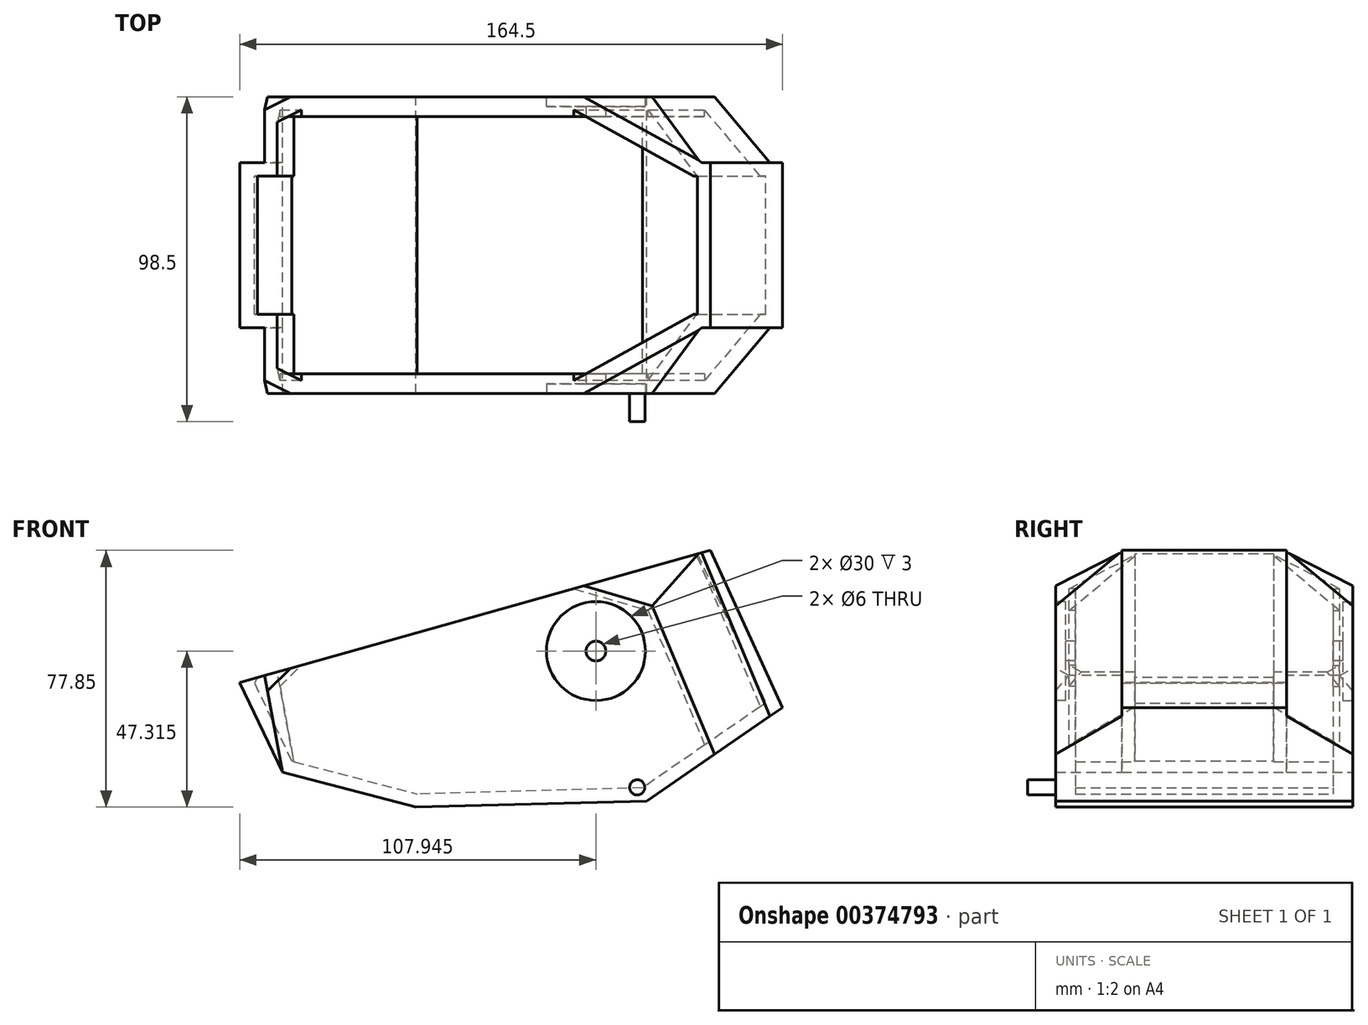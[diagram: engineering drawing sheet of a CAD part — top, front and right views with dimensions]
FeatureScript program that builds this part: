
annotation { "Feature Type Name" : "Feature", "Feature Type Description" : "" }
export const myFeature = defineFeature(function(context is Context, id is Id, definition is map)
    precondition{}
    {
        {
            var Q0;
            Q0=qCreatedBy(makeId("Front.planeOp"),FACE);
            var sketch = newSketch(context, id + "F0", { "sketchPlane" : qUnion([Q0])});
            skLineSegment(sketch, "E0", {"start": v(59.84, 44.16) * mm, "end": v(16.91, 57.67) * mm});
            skLineSegment(sketch, "E1", {"start": v(16.91, 57.67) * mm, "end": v(-68.9, 30.57) * mm});
            skLineSegment(sketch, "E2", {"start": v(-68.9, 30.57) * mm, "end": v(-82.75, 3.95) * mm});
            skLineSegment(sketch, "E3", {"start": v(-82.75, 3.95) * mm, "end": v(-69.82, -23.12) * mm});
            skLineSegment(sketch, "E4", {"start": v(-69.82, -23.12) * mm, "end": v(-29.42, -33.71) * mm});
            skLineSegment(sketch, "E5", {"start": v(59.84, 44.16) * mm, "end": v(-82.75, 3.95) * mm});
            skLineSegment(sketch, "E6", {"start": v(59.84, 44.16) * mm, "end": v(-205.25, -30.6) * mm, "construction": true});
            skLineSegment(sketch, "E7", {"start": v(81.75, -3.5) * mm, "end": v(40.56, -31.85) * mm});
            skLineSegment(sketch, "E8", {"start": v(59.84, 44.16) * mm, "end": v(81.75, -3.5) * mm});
            skLineSegment(sketch, "E9", {"start": v(40.56, -31.85) * mm, "end": v(-29.42, -33.71) * mm});
            skPoint(sketch, "E10", {"position": v(57.24, -20.37) * mm});
            skSolve(sketch);
        }
        {
            var Q0;
            Q0 = qSketchRegion(id + "F0", true);
            extrude(context, id + "F1", {"entities" : qUnion([Q0]), "depth" : 50 * mm, "offsetDistance" : 25 * mm});
        }
        {
            var Q0;
            Q0=makeQuery(id+"F1.opExtrude","CAP_FACE",FACE,{"disambiguationData":[OSD([sQuery(id+"F0.wireOp",EDGE,"bDbODIuM-1u16-Aznj-rPBm-DqaUrzULmyHa"),sQuery(id+"F0.wireOp",EDGE,"UB7G52HZ-YFA2-uVYt-4jSg-YKdLqot3CmFC"),sQuery(id+"F0.wireOp",EDGE,"E0"),sQuery(id+"F0.wireOp",EDGE,"E1"),sQuery(id+"F0.wireOp",EDGE,"E2"),sQuery(id+"F0.wireOp",EDGE,"E3"),sQuery(id+"F0.wireOp",EDGE,"evsTFQqy-KAtR-kOSi-w0PH-wNtTzoorWs0J"),sQuery(id+"F0.wireOp",EDGE,"E4")])],"isStart":false});
            var sketch = newSketch(context, id + "F2", { "sketchPlane" : qUnion([Q0])});
            skLineSegment(sketch, "E11", {"start": v(-69.82, -23.12) * mm, "end": v(61.15, -17.68) * mm, "construction": true});
            skLineSegment(sketch, "E12", {"start": v(61.15, -17.68) * mm, "end": v(42.24, 27.3) * mm});
            skLineSegment(sketch, "E13", {"start": v(42.24, 27.3) * mm, "end": v(9.45, 36.88) * mm});
            skLineSegment(sketch, "E14", {"start": v(9.45, 36.88) * mm, "end": v(-60.14, 15.5) * mm});
            skLineSegment(sketch, "E15", {"start": v(-60.14, 15.5) * mm, "end": v(-74.38, 1.46) * mm});
            skLineSegment(sketch, "E16", {"start": v(-74.38, 1.46) * mm, "end": v(-69.82, -23.12) * mm});
            skSolve(sketch);
        }
        {
            var Q0;
            Q0=makeQuery(id+"F2.imprint","IMPRINT",FACE,{"disambiguationData":[TD([[makeQuery(id+"F2.imprint","IMPRINT",EDGE,{"derivedFrom":sQuery(id+"F2.wireOp",EDGE,"E12")}),1.0]])]});
            extrude(context, id + "F3", {"entities" : qUnion([Q0]), "operationType" : NewBodyOperationType.ADD, "depth" : 20 * mm, "offsetDistance" : 25 * mm, "hasSecondDirection" : true, "secondDirectionOppositeDirection" : true, "secondDirectionDepth" : (20 + 50) * mm});
        }
        {
            var Q0;
            Q0=makeQuery(id+"F3.boolean.opBoolean","INTERSECT",EDGE,{"derivedFrom":[makeQuery(id+"F1.opExtrude","CAP_FACE",FACE,{"disambiguationData":[OSD([sQuery(id+"F0.wireOp",EDGE,"bDbODIuM-1u16-Aznj-rPBm-DqaUrzULmyHa"),sQuery(id+"F0.wireOp",EDGE,"UB7G52HZ-YFA2-uVYt-4jSg-YKdLqot3CmFC"),sQuery(id+"F0.wireOp",EDGE,"E0"),sQuery(id+"F0.wireOp",EDGE,"E1"),sQuery(id+"F0.wireOp",EDGE,"E2"),sQuery(id+"F0.wireOp",EDGE,"E3"),sQuery(id+"F0.wireOp",EDGE,"evsTFQqy-KAtR-kOSi-w0PH-wNtTzoorWs0J"),sQuery(id+"F0.wireOp",EDGE,"E4")])],"isStart":true}),makeQuery(id+"F3.opExtrude","SWEPT_FACE",FACE,{"disambiguationData":[OSD([sQuery(id+"F2.wireOp",EDGE,"E14")])]})]});
            var Q1;
            Q1=makeQuery(id+"F3.boolean.opBoolean","INTERSECT",EDGE,{"derivedFrom":[makeQuery(id+"F1.opExtrude","CAP_FACE",FACE,{"disambiguationData":[OSD([sQuery(id+"F0.wireOp",EDGE,"bDbODIuM-1u16-Aznj-rPBm-DqaUrzULmyHa"),sQuery(id+"F0.wireOp",EDGE,"UB7G52HZ-YFA2-uVYt-4jSg-YKdLqot3CmFC"),sQuery(id+"F0.wireOp",EDGE,"E0"),sQuery(id+"F0.wireOp",EDGE,"E1"),sQuery(id+"F0.wireOp",EDGE,"E2"),sQuery(id+"F0.wireOp",EDGE,"E3"),sQuery(id+"F0.wireOp",EDGE,"evsTFQqy-KAtR-kOSi-w0PH-wNtTzoorWs0J"),sQuery(id+"F0.wireOp",EDGE,"E4")])],"isStart":true}),makeQuery(id+"F3.opExtrude","SWEPT_FACE",FACE,{"disambiguationData":[OSD([sQuery(id+"F2.wireOp",EDGE,"E13")])]})]});
            var Q2;
            Q2=makeQuery(id+"F3.boolean.opBoolean","INTERSECT",EDGE,{"derivedFrom":[makeQuery(id+"F1.opExtrude","CAP_FACE",FACE,{"disambiguationData":[OSD([sQuery(id+"F0.wireOp",EDGE,"bDbODIuM-1u16-Aznj-rPBm-DqaUrzULmyHa"),sQuery(id+"F0.wireOp",EDGE,"UB7G52HZ-YFA2-uVYt-4jSg-YKdLqot3CmFC"),sQuery(id+"F0.wireOp",EDGE,"E0"),sQuery(id+"F0.wireOp",EDGE,"E1"),sQuery(id+"F0.wireOp",EDGE,"E2"),sQuery(id+"F0.wireOp",EDGE,"E3"),sQuery(id+"F0.wireOp",EDGE,"evsTFQqy-KAtR-kOSi-w0PH-wNtTzoorWs0J"),sQuery(id+"F0.wireOp",EDGE,"E4")])],"isStart":true}),makeQuery(id+"F3.opExtrude","SWEPT_FACE",FACE,{"disambiguationData":[OSD([sQuery(id+"F2.wireOp",EDGE,"E15")])]})]});
            var Q3;
            Q3=makeQuery(id+"F3.boolean.opBoolean","INTERSECT",EDGE,{"derivedFrom":[makeQuery(id+"F1.opExtrude","CAP_FACE",FACE,{"disambiguationData":[OSD([sQuery(id+"F0.wireOp",EDGE,"bDbODIuM-1u16-Aznj-rPBm-DqaUrzULmyHa"),sQuery(id+"F0.wireOp",EDGE,"UB7G52HZ-YFA2-uVYt-4jSg-YKdLqot3CmFC"),sQuery(id+"F0.wireOp",EDGE,"E0"),sQuery(id+"F0.wireOp",EDGE,"E1"),sQuery(id+"F0.wireOp",EDGE,"E2"),sQuery(id+"F0.wireOp",EDGE,"E3"),sQuery(id+"F0.wireOp",EDGE,"evsTFQqy-KAtR-kOSi-w0PH-wNtTzoorWs0J"),sQuery(id+"F0.wireOp",EDGE,"E4")])],"isStart":true}),makeQuery(id+"F3.opExtrude","SWEPT_FACE",FACE,{"disambiguationData":[OSD([sQuery(id+"F2.wireOp",EDGE,"E12")])]})]});
            chamfer(context, id + "F4", {"entities" : qUnion([Q0, Q1, Q2, Q3]), "chamferType" : ChamferType.OFFSET_ANGLE, "width" : 20 * mm, "oppositeDirection" : false, "angle" : 45 * degree, "tangentPropagation" : true});
        }
        {
            var Q0;
            Q0=makeQuery(id+"F3.boolean.opBoolean","INTERSECT",EDGE,{"derivedFrom":[makeQuery(id+"F1.opExtrude","CAP_FACE",FACE,{"disambiguationData":[OSD([sQuery(id+"F0.wireOp",EDGE,"bDbODIuM-1u16-Aznj-rPBm-DqaUrzULmyHa"),sQuery(id+"F0.wireOp",EDGE,"UB7G52HZ-YFA2-uVYt-4jSg-YKdLqot3CmFC"),sQuery(id+"F0.wireOp",EDGE,"E0"),sQuery(id+"F0.wireOp",EDGE,"E1"),sQuery(id+"F0.wireOp",EDGE,"E2"),sQuery(id+"F0.wireOp",EDGE,"E3"),sQuery(id+"F0.wireOp",EDGE,"evsTFQqy-KAtR-kOSi-w0PH-wNtTzoorWs0J"),sQuery(id+"F0.wireOp",EDGE,"E4")])],"isStart":false}),makeQuery(id+"F3.opExtrude","SWEPT_FACE",FACE,{"disambiguationData":[OSD([sQuery(id+"F2.wireOp",EDGE,"E13")])]})]});
            var Q1;
            Q1=makeQuery(id+"F3.boolean.opBoolean","INTERSECT",EDGE,{"derivedFrom":[makeQuery(id+"F1.opExtrude","CAP_FACE",FACE,{"disambiguationData":[OSD([sQuery(id+"F0.wireOp",EDGE,"bDbODIuM-1u16-Aznj-rPBm-DqaUrzULmyHa"),sQuery(id+"F0.wireOp",EDGE,"UB7G52HZ-YFA2-uVYt-4jSg-YKdLqot3CmFC"),sQuery(id+"F0.wireOp",EDGE,"E0"),sQuery(id+"F0.wireOp",EDGE,"E1"),sQuery(id+"F0.wireOp",EDGE,"E2"),sQuery(id+"F0.wireOp",EDGE,"E3"),sQuery(id+"F0.wireOp",EDGE,"evsTFQqy-KAtR-kOSi-w0PH-wNtTzoorWs0J"),sQuery(id+"F0.wireOp",EDGE,"E4")])],"isStart":false}),makeQuery(id+"F3.opExtrude","SWEPT_FACE",FACE,{"disambiguationData":[OSD([sQuery(id+"F2.wireOp",EDGE,"E14")])]})]});
            var Q2;
            Q2=makeQuery(id+"F3.boolean.opBoolean","INTERSECT",EDGE,{"derivedFrom":[makeQuery(id+"F1.opExtrude","CAP_FACE",FACE,{"disambiguationData":[OSD([sQuery(id+"F0.wireOp",EDGE,"bDbODIuM-1u16-Aznj-rPBm-DqaUrzULmyHa"),sQuery(id+"F0.wireOp",EDGE,"UB7G52HZ-YFA2-uVYt-4jSg-YKdLqot3CmFC"),sQuery(id+"F0.wireOp",EDGE,"E0"),sQuery(id+"F0.wireOp",EDGE,"E1"),sQuery(id+"F0.wireOp",EDGE,"E2"),sQuery(id+"F0.wireOp",EDGE,"E3"),sQuery(id+"F0.wireOp",EDGE,"evsTFQqy-KAtR-kOSi-w0PH-wNtTzoorWs0J"),sQuery(id+"F0.wireOp",EDGE,"E4")])],"isStart":false}),makeQuery(id+"F3.opExtrude","SWEPT_FACE",FACE,{"disambiguationData":[OSD([sQuery(id+"F2.wireOp",EDGE,"E12")])]})]});
            var Q3;
            Q3=makeQuery(id+"F3.boolean.opBoolean","INTERSECT",EDGE,{"derivedFrom":[makeQuery(id+"F1.opExtrude","CAP_FACE",FACE,{"disambiguationData":[OSD([sQuery(id+"F0.wireOp",EDGE,"bDbODIuM-1u16-Aznj-rPBm-DqaUrzULmyHa"),sQuery(id+"F0.wireOp",EDGE,"UB7G52HZ-YFA2-uVYt-4jSg-YKdLqot3CmFC"),sQuery(id+"F0.wireOp",EDGE,"E0"),sQuery(id+"F0.wireOp",EDGE,"E1"),sQuery(id+"F0.wireOp",EDGE,"E2"),sQuery(id+"F0.wireOp",EDGE,"E3"),sQuery(id+"F0.wireOp",EDGE,"evsTFQqy-KAtR-kOSi-w0PH-wNtTzoorWs0J"),sQuery(id+"F0.wireOp",EDGE,"E4")])],"isStart":false}),makeQuery(id+"F3.opExtrude","SWEPT_FACE",FACE,{"disambiguationData":[OSD([sQuery(id+"F2.wireOp",EDGE,"E15")])]})]});
            chamfer(context, id + "F5", {"entities" : qUnion([Q0, Q1, Q2, Q3]), "chamferType" : ChamferType.OFFSET_ANGLE, "width" : 20 * mm, "oppositeDirection" : false, "angle" : 45 * degree, "tangentPropagation" : true});
        }
        {
            var Q0;
            Q0=makeQuery(id+"F1.opExtrude","SWEPT_EDGE",EDGE,{"disambiguationData":[OSD([sQuery(id+"F0.wireOp",EDGE,"E0"),sQuery(id+"F0.wireOp",EDGE,"E1")])]});
            cPlane(context, id + "F6", {"entities" : qUnion([Q0]), "cplaneType" : CPlaneType.MID_PLANE, "offset" : 25 * mm, "width" : 150 * mm, "height" : 150 * mm});
        }
        {
            var Q0;
            Q0=qCreatedBy(id+"F6.planeOp",FACE);
            var sketch = newSketch(context, id + "F7", { "sketchPlane" : qUnion([Q0])});
            skLineSegment(sketch, "E17", {"start": v(107.63, -2.94) * mm, "end": v(-40.6, 38.73) * mm});
            skLineSegment(sketch, "E18", {"start": v(-40.6, 38.73) * mm, "end": v(-63.04, 45.04) * mm});
            skLineSegment(sketch, "E19", {"start": v(-63.04, 45.04) * mm, "end": v(41.08, 93.89) * mm});
            skLineSegment(sketch, "E20", {"start": v(41.08, 93.89) * mm, "end": v(107.63, -2.94) * mm});
            skSolve(sketch);
        }
        {
            var Q0;
            Q0=makeQuery(id+"F7.imprint","IMPRINT",FACE,{"disambiguationData":[TD([[makeQuery(id+"F7.imprint","IMPRINT",EDGE,{"derivedFrom":sQuery(id+"F7.wireOp",EDGE,"E17")}),-1.0]])]});
            extrude(context, id + "F8", {"entities" : qUnion([Q0]), "operationType" : NewBodyOperationType.REMOVE, "oppositeDirection" : true, "depth" : 56 * mm, "offsetDistance" : 25 * mm, "hasSecondDirection" : true, "secondDirectionOppositeDirection" : false, "secondDirectionDepth" : 80 * mm});
        }
        {
            var Q0;
            Q0=makeQuery(id+"F8.boolean.opBoolean","COPY",FACE,{"derivedFrom":makeQuery(id+"F8.opExtrude","SWEPT_FACE",FACE,{"disambiguationData":[OSD([sQuery(id+"F7.wireOp",EDGE,"E17"),sQuery(id+"F7.wireOp",EDGE,"E18")])]})});
            shell(context, id + "F9", {"entities" : qUnion([Q0]), "thickness" : 4 * mm});
        }
        {
            var Q0;
            Q0=makeQuery(id+"F3.opExtrude","CAP_FACE",FACE,{"disambiguationData":[OSD([sQuery(id+"F0.wireOp",EDGE,"E4"),sQuery(id+"F0.wireOp",EDGE,"E7"),sQuery(id+"F0.wireOp",EDGE,"E9"),sQuery(id+"F2.wireOp",EDGE,"E12"),sQuery(id+"F2.wireOp",EDGE,"E13"),sQuery(id+"F2.wireOp",EDGE,"E14"),sQuery(id+"F2.wireOp",EDGE,"E15"),sQuery(id+"F2.wireOp",EDGE,"E16")])],"isStart":true});
            var sketch = newSketch(context, id + "F10", { "sketchPlane" : qUnion([Q0])});
            skLineSegment(sketch, "E21", {"start": v(-21.5, 33.36) * mm, "end": v(-40.56, -31.85) * mm, "construction": true});
            skPoint(sketch, "E22", {"position": v(-27.11, 14.17) * mm});
            skLineSegment(sketch, "E23", {"start": v(-27.11, 14.17) * mm, "end": v(6.72, 4.28) * mm});
            skPoint(sketch, "E24", {"position": v(-25.2, 13.6) * mm});
            skCircle(sketch, "E25", {"center": v(-25.2, 13.6) * mm, "radius": 15 * mm});
            skSolve(sketch);
        }
        {
            var Q0;
            Q0=makeQuery(id+"F10.imprint","IMPRINT",FACE,{"disambiguationData":[TD([[makeQuery(id+"F10.imprint","IMPRINT",EDGE,{"derivedFrom":sQuery(id+"F10.wireOp",EDGE,"E25")}),1.0]])]});
            extrude(context, id + "F11", {"entities" : qUnion([Q0]), "operationType" : NewBodyOperationType.REMOVE, "oppositeDirection" : true, "depth" : 3 * mm, "offsetDistance" : 25 * mm});
        }
        {
            var Q0;
            Q0=makeQuery(id+"F3.opExtrude","CAP_FACE",FACE,{"disambiguationData":[OSD([sQuery(id+"F0.wireOp",EDGE,"E4"),sQuery(id+"F0.wireOp",EDGE,"E7"),sQuery(id+"F0.wireOp",EDGE,"E9"),sQuery(id+"F2.wireOp",EDGE,"E12"),sQuery(id+"F2.wireOp",EDGE,"E13"),sQuery(id+"F2.wireOp",EDGE,"E14"),sQuery(id+"F2.wireOp",EDGE,"E15"),sQuery(id+"F2.wireOp",EDGE,"E16")])],"isStart":false});
            var sketch = newSketch(context, id + "F12", { "sketchPlane" : qUnion([Q0])});
            skLineSegment(sketch, "E26", {"start": v(21.5, 33.36) * mm, "end": v(40.56, -31.85) * mm, "construction": true});
            skPoint(sketch, "E27", {"position": v(27.11, 14.17) * mm});
            skLineSegment(sketch, "E28", {"start": v(27.11, 14.17) * mm, "end": v(4.6, 7.59) * mm});
            skPoint(sketch, "E29", {"position": v(25.2, 13.6) * mm});
            skCircle(sketch, "E30", {"center": v(25.2, 13.6) * mm, "radius": 15 * mm});
            skSolve(sketch);
        }
        {
            var Q0;
            Q0=makeQuery(id+"F12.imprint","IMPRINT",FACE,{"disambiguationData":[TD([[makeQuery(id+"F12.imprint","IMPRINT",EDGE,{"derivedFrom":sQuery(id+"F12.wireOp",EDGE,"E30")}),1.0]])]});
            extrude(context, id + "F13", {"entities" : qUnion([Q0]), "operationType" : NewBodyOperationType.REMOVE, "oppositeDirection" : true, "depth" : 3 * mm, "offsetDistance" : 25 * mm});
        }
        {
            var Q0;
            Q0=makeQuery(id+"F3.opExtrude","CAP_FACE",FACE,{"disambiguationData":[OSD([sQuery(id+"F0.wireOp",EDGE,"E4"),sQuery(id+"F0.wireOp",EDGE,"E7"),sQuery(id+"F0.wireOp",EDGE,"E9"),sQuery(id+"F2.wireOp",EDGE,"E12"),sQuery(id+"F2.wireOp",EDGE,"E13"),sQuery(id+"F2.wireOp",EDGE,"E14"),sQuery(id+"F2.wireOp",EDGE,"E15"),sQuery(id+"F2.wireOp",EDGE,"E16")])],"isStart":false});
            var sketch = newSketch(context, id + "F14", { "sketchPlane" : qUnion([Q0])});
            skLineSegment(sketch, "E31", {"start": v(40.56, -31.85) * mm, "end": v(37.72, -27.73) * mm});
            skCircle(sketch, "E32", {"center": v(37.72, -27.73) * mm, "radius": 2.3 * mm});
            skSolve(sketch);
        }
        {
            var Q0;
            Q0=makeQuery(id+"F14.imprint","IMPRINT",FACE,{"disambiguationData":[TD([[makeQuery(id+"F14.imprint","IMPRINT",EDGE,{"derivedFrom":sQuery(id+"F14.wireOp",EDGE,"E32")}),1.0]])]});
            extrude(context, id + "F15", {"entities" : qUnion([Q0]), "operationType" : NewBodyOperationType.ADD, "depth" : 5.4 * mm, "offsetDistance" : 25 * mm});
        }
        {
            var Q0;
            Q0=makeQuery(id+"F13.boolean.opBoolean","COPY",FACE,{"derivedFrom":makeQuery(id+"F13.opExtrude","CAP_FACE",FACE,{"disambiguationData":[OSD([sQuery(id+"F12.wireOp",EDGE,"E30")])],"isStart":false})});
            var sketch = newSketch(context, id + "F16", { "sketchPlane" : qUnion([Q0])});
            skCircle(sketch, "E33", {"center": v(25.2, 13.6) * mm, "radius": 3 * mm});
            skSolve(sketch);
        }
        {
            var Q0;
            Q0=makeQuery(id+"F16.imprint","IMPRINT",FACE,{"disambiguationData":[TD([[makeQuery(id+"F16.imprint","IMPRINT",EDGE,{"derivedFrom":sQuery(id+"F16.wireOp",EDGE,"E33")}),1.0]])]});
            extrude(context, id + "F17", {"entities" : qUnion([Q0]), "operationType" : NewBodyOperationType.REMOVE, "oppositeDirection" : true, "depth" : 124 * mm, "offsetDistance" : 25 * mm});
        }
        {
            var Q0;
            {var subQ0=sQuery(id+"F2.wireOp",EDGE,"E16");var subQ1=sQuery(id+"F2.wireOp",EDGE,"E15");var subQ2=sQuery(id+"F2.wireOp",EDGE,"E14");var subQ3=sQuery(id+"F2.wireOp",EDGE,"E13");var subQ4=sQuery(id+"F2.wireOp",EDGE,"E12");var subQ5=sQuery(id+"F0.wireOp",EDGE,"E9");var subQ6=sQuery(id+"F0.wireOp",EDGE,"E7");var subQ7=sQuery(id+"F0.wireOp",EDGE,"E4");Q0=makeQuery(id+"F9.opShell","OFFSET_FACE",FACE,{"disambiguationData":[OSD([subQ7,subQ6,subQ5,subQ4,subQ3,subQ2,subQ1,subQ0]),TDD([makeQuery(id+"F3.opExtrude","CAP_FACE",FACE,{"disambiguationData":[OSD([subQ7,subQ6,subQ5,subQ4,subQ3,subQ2,subQ1,subQ0])],"isStart":true})])]});}
            extrude(context, id + "F18", {"entities" : qUnion([Q0]), "operationType" : NewBodyOperationType.ADD, "depth" : 2 * mm, "offsetDistance" : 25 * mm});
        }
        {
            var Q0;
            {var subQ0=sQuery(id+"F2.wireOp",EDGE,"E16");var subQ1=sQuery(id+"F2.wireOp",EDGE,"E15");var subQ2=sQuery(id+"F2.wireOp",EDGE,"E14");var subQ3=sQuery(id+"F2.wireOp",EDGE,"E13");var subQ4=sQuery(id+"F2.wireOp",EDGE,"E12");var subQ5=sQuery(id+"F0.wireOp",EDGE,"E9");var subQ6=sQuery(id+"F0.wireOp",EDGE,"E7");var subQ7=sQuery(id+"F0.wireOp",EDGE,"E4");Q0=makeQuery(id+"F9.opShell","OFFSET_FACE",FACE,{"disambiguationData":[OSD([subQ7,subQ6,subQ5,subQ4,subQ3,subQ2,subQ1,subQ0]),TDD([makeQuery(id+"F3.opExtrude","CAP_FACE",FACE,{"disambiguationData":[OSD([subQ7,subQ6,subQ5,subQ4,subQ3,subQ2,subQ1,subQ0])],"isStart":false})])]});}
            extrude(context, id + "F19", {"entities" : qUnion([Q0]), "operationType" : NewBodyOperationType.ADD, "depth" : 2 * mm, "offsetDistance" : 25 * mm});
        }
        {
            var Q0;
            Q0=makeQuery(id+"F15.opExtrude","CAP_FACE",FACE,{"disambiguationData":[OSD([sQuery(id+"F14.wireOp",EDGE,"E32")])],"isStart":false});
            extrude(context, id + "F20", {"entities" : qUnion([Q0]), "operationType" : NewBodyOperationType.ADD, "depth" : 3.1 * mm, "offsetDistance" : 25 * mm});
        }
    });
